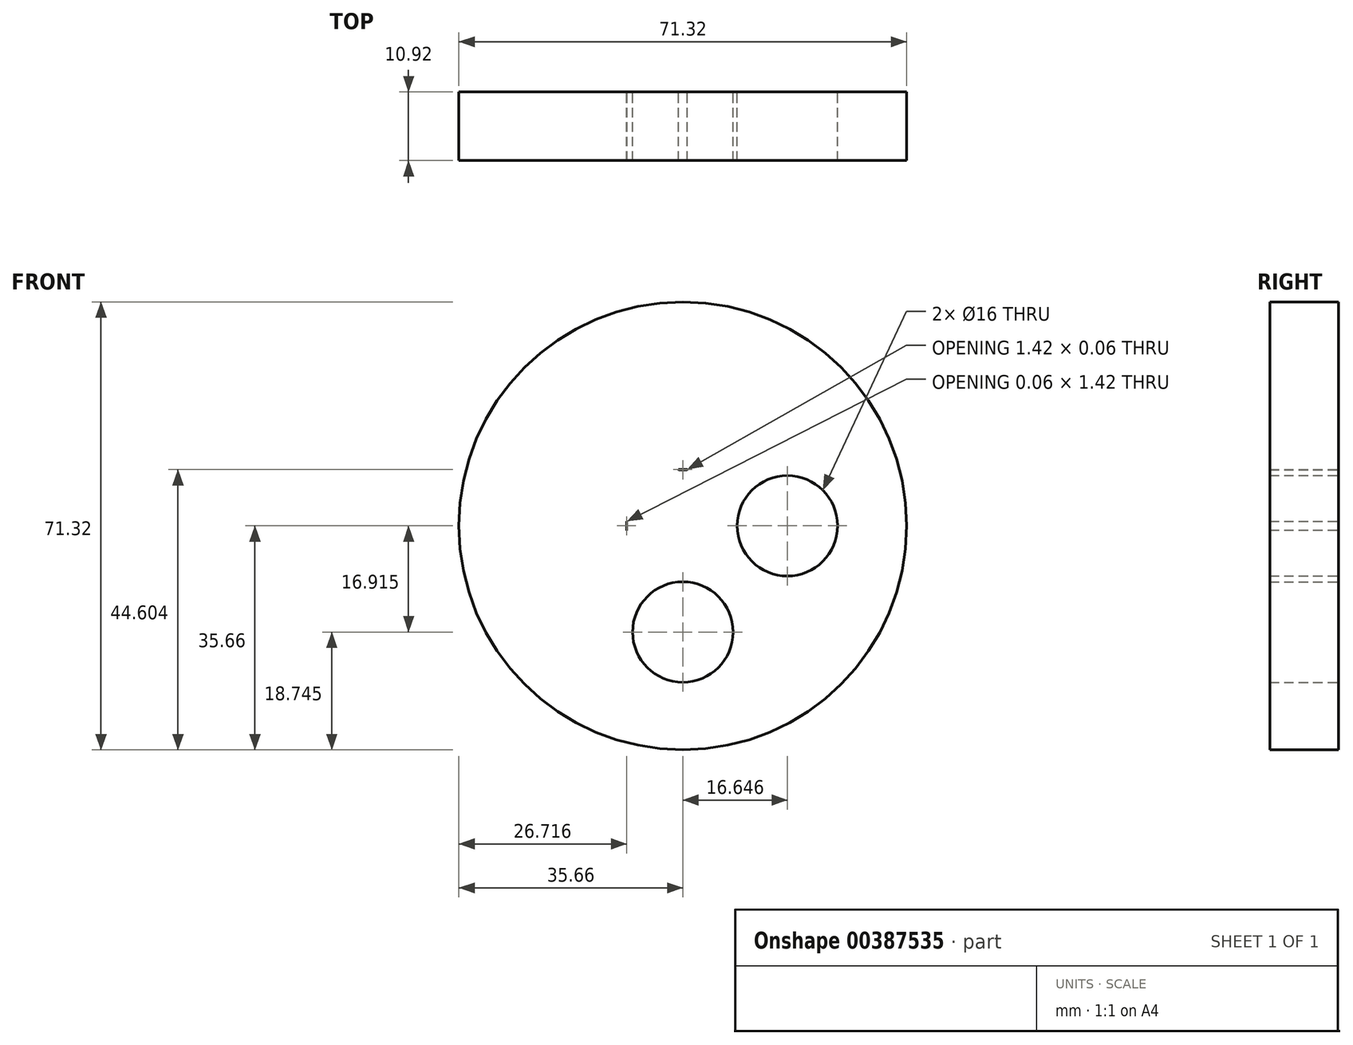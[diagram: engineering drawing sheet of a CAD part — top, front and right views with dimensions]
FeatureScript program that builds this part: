
annotation { "Feature Type Name" : "Feature", "Feature Type Description" : "" }
export const myFeature = defineFeature(function(context is Context, id is Id, definition is map)
    precondition{}
    {
        {
            var Q0;
            Q0=qCreatedBy(makeId("Front.planeOp"),FACE);
            var sketch = newSketch(context, id + "F0", { "sketchPlane" : qUnion([Q0])});
            skCircle(sketch, "E0", {"center": v(0, 0) * mm, "radius": 6.34 * mm});
            skCircle(sketch, "E1", {"center": v(0, 0) * mm, "radius": 8.97 * mm});
            skCircle(sketch, "E2", {"center": v(-16.91, 0) * mm, "radius": 8 * mm});
            skCircle(sketch, "E3", {"center": v(0, 16.91) * mm, "radius": 8 * mm});
            skCircle(sketch, "E4", {"center": v(16.65, 0) * mm, "radius": 8 * mm});
            skCircle(sketch, "E5", {"center": v(0, -16.91) * mm, "radius": 8 * mm});
            skCircle(sketch, "E6", {"center": v(0, 0) * mm, "radius": 30.24 * mm});
            skCircle(sketch, "E7", {"center": v(0, 0) * mm, "radius": 35.66 * mm});
            skSolve(sketch);
        }
        {
            var Q0;
            Q0 = qSketchRegion(id + "F0", true);
            var Q1;
            {var subQ0=sQuery(id+"F0.wireOp",EDGE,"E3");var subQ1=sQuery(id+"F0.wireOp",EDGE,"E1");var subQ2=makeQuery(id+"F0.imprint","INTERSECT",VERTEX,{"disambiguationData":[OD(0.0)],"derivedFrom":[subQ1,subQ0]});Q1=makeQuery(id+"F0.imprint","IMPRINT",FACE,{"disambiguationData":[TD([[makeQuery(id+"F0.imprint","IMPRINT",EDGE,{"disambiguationData":[TD([[subQ2,-1.0]])],"derivedFrom":subQ1}),-1.0]])]});}
            var Q2;
            Q2=makeQuery(id+"F0.imprint","IMPRINT",FACE,{"disambiguationData":[TD([[makeQuery(id+"F0.imprint","IMPRINT",EDGE,{"derivedFrom":sQuery(id+"F0.wireOp",EDGE,"E0")}),-1.0]])]});
            var Q3;
            {var subQ0=sQuery(id+"F0.wireOp",EDGE,"E4");var subQ1=sQuery(id+"F0.wireOp",EDGE,"E1");var subQ2=makeQuery(id+"F0.imprint","INTERSECT",VERTEX,{"disambiguationData":[OD(0.0)],"derivedFrom":[subQ1,subQ0]});Q3=makeQuery(id+"F0.imprint","IMPRINT",FACE,{"disambiguationData":[TD([[makeQuery(id+"F0.imprint","IMPRINT",EDGE,{"disambiguationData":[TD([[subQ2,1.0]])],"derivedFrom":subQ1}),-1.0]])]});}
            var Q4;
            {var subQ0=sQuery(id+"F0.wireOp",EDGE,"E2");var subQ1=sQuery(id+"F0.wireOp",EDGE,"E1");var subQ2=makeQuery(id+"F0.imprint","INTERSECT",VERTEX,{"disambiguationData":[OD(0.0)],"derivedFrom":[subQ1,subQ0]});Q4=makeQuery(id+"F0.imprint","IMPRINT",FACE,{"disambiguationData":[TD([[makeQuery(id+"F0.imprint","IMPRINT",EDGE,{"disambiguationData":[TD([[subQ2,-1.0]])],"derivedFrom":subQ1}),-1.0]])]});}
            var Q5;
            {var subQ0=sQuery(id+"F0.wireOp",EDGE,"E5");var subQ1=sQuery(id+"F0.wireOp",EDGE,"E1");var subQ2=makeQuery(id+"F0.imprint","INTERSECT",VERTEX,{"disambiguationData":[OD(0.0)],"derivedFrom":[subQ1,subQ0]});Q5=makeQuery(id+"F0.imprint","IMPRINT",FACE,{"disambiguationData":[TD([[makeQuery(id+"F0.imprint","IMPRINT",EDGE,{"disambiguationData":[TD([[subQ2,-1.0]])],"derivedFrom":subQ1}),-1.0]])]});}
            var Q6;
            Q6=makeQuery(id+"F0.imprint","IMPRINT",FACE,{"disambiguationData":[TD([[makeQuery(id+"F0.imprint","IMPRINT",EDGE,{"derivedFrom":sQuery(id+"F0.wireOp",EDGE,"E0")}),1.0]])]});
            extrude(context, id + "F1", {"entities" : qUnion([Q0, Q1, Q2, Q3, Q4, Q5, Q6]), "depth" : 10.92 * mm});
        }
    });
